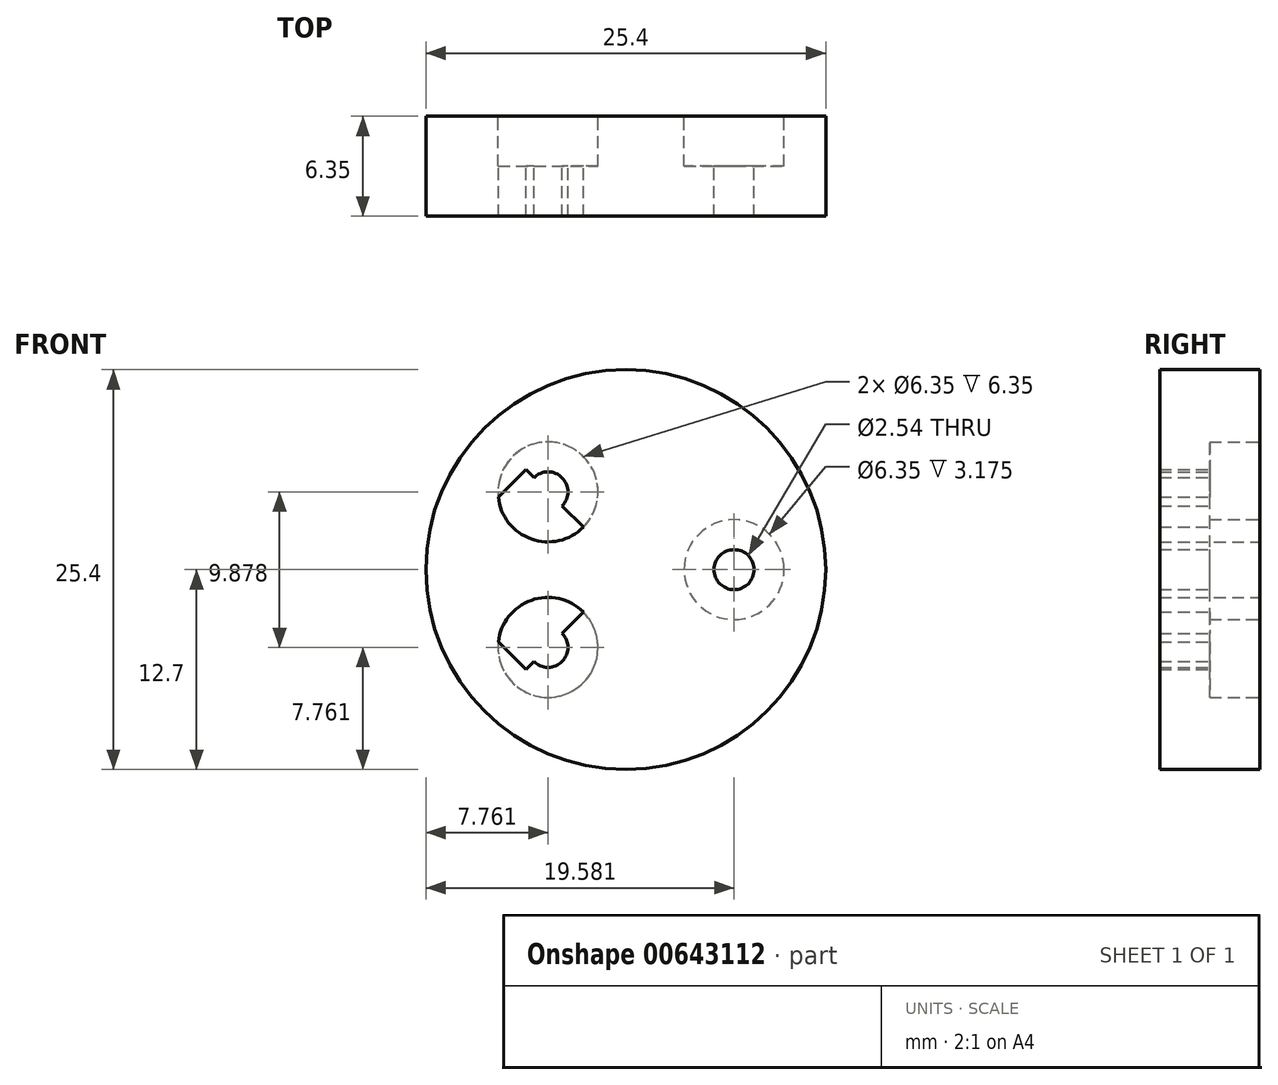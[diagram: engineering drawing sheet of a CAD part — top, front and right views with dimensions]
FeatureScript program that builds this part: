
annotation { "Feature Type Name" : "Feature", "Feature Type Description" : "" }
export const myFeature = defineFeature(function(context is Context, id is Id, definition is map)
    precondition{}
    {
        {
            var Q0;
            Q0=qCreatedBy(makeId("Front.planeOp"),FACE);
            var sketch = newSketch(context, id + "F0", { "sketchPlane" : qUnion([Q0])});
            skCircle(sketch, "E0", {"center": v(0, 0) * mm, "radius": 12.7 * mm});
            skCircle(sketch, "E1", {"center": v(-4.94, 4.94) * mm, "radius": 3.18 * mm});
            skCircle(sketch, "E2", {"center": v(-4.94, -4.94) * mm, "radius": 3.18 * mm});
            skCircle(sketch, "E3", {"center": v(6.88, 0) * mm, "radius": 3.18 * mm});
            skLineSegment(sketch, "E4", {"start": v(0, 12.7) * mm, "end": v(0, -12.7) * mm});
            skLineSegment(sketch, "E5", {"start": v(0, -12.7) * mm, "end": v(0, 0) * mm});
            skLineSegment(sketch, "E6", {"start": v(-12.7, 0) * mm, "end": v(0, 0) * mm});
            skLineSegment(sketch, "E7", {"start": v(12.7, 0) * mm, "end": v(0, 0) * mm});
            skLineSegment(sketch, "E8", {"start": v(0, 12.7) * mm, "end": v(-12.7, 0) * mm});
            skLineSegment(sketch, "E9", {"start": v(0, 0) * mm, "end": v(-6.35, 6.35) * mm});
            skLineSegment(sketch, "E10", {"start": v(-12.7, 0) * mm, "end": v(0, -12.7) * mm});
            skLineSegment(sketch, "E11", {"start": v(0, 0) * mm, "end": v(-6.35, -6.35) * mm});
            skCircle(sketch, "E12", {"center": v(-4.94, 4.94) * mm, "radius": 1.27 * mm});
            skCircle(sketch, "E13", {"center": v(6.88, 0) * mm, "radius": 1.27 * mm});
            skCircle(sketch, "E14", {"center": v(-4.94, -4.94) * mm, "radius": 1.27 * mm});
            skSolve(sketch);
        }
        {
            var Q0;
            Q0 = qSketchRegion(id + "F0", true);
            var Q1;
            {var subQ1=sQuery(id+"F0.wireOp",EDGE,"E8");var subQ5=sQuery(id+"F0.wireOp",EDGE,"E1");var subQ6=makeQuery(id+"F0.imprint","INTERSECT",VERTEX,{"disambiguationData":[OD(0.0)],"derivedFrom":[subQ5,subQ1]});Q1=makeQuery(id+"F0.imprint","IMPRINT",FACE,{"disambiguationData":[TD([[makeQuery(id+"F0.imprint","IMPRINT",EDGE,{"disambiguationData":[TD([[subQ6,-1.0]])],"derivedFrom":subQ5}),1.0]])]});}
            var Q2;
            {var subQ1=sQuery(id+"F0.wireOp",EDGE,"E8");var subQ5=sQuery(id+"F0.wireOp",EDGE,"E1");var subQ8=makeQuery(id+"F0.imprint","INTERSECT",VERTEX,{"disambiguationData":[OD(1.0)],"derivedFrom":[subQ5,subQ1]});Q2=makeQuery(id+"F0.imprint","IMPRINT",FACE,{"disambiguationData":[TD([[makeQuery(id+"F0.imprint","IMPRINT",EDGE,{"disambiguationData":[TD([[subQ8,1.0]])],"derivedFrom":subQ5}),1.0]])]});}
            var Q3;
            {var subQ0=sQuery(id+"F0.wireOp",EDGE,"E8");var subQ1=sQuery(id+"F0.wireOp",EDGE,"E1");var subQ2=makeQuery(id+"F0.imprint","INTERSECT",VERTEX,{"disambiguationData":[OD(0.0)],"derivedFrom":[subQ1,subQ0]});Q3=makeQuery(id+"F0.imprint","IMPRINT",FACE,{"disambiguationData":[TD([[makeQuery(id+"F0.imprint","IMPRINT",EDGE,{"disambiguationData":[TD([[subQ2,1.0]])],"derivedFrom":subQ1}),1.0]])]});}
            var Q4;
            {var subQ0=sQuery(id+"F0.wireOp",EDGE,"E7");var subQ1=sQuery(id+"F0.wireOp",EDGE,"E3");var subQ2=makeQuery(id+"F0.imprint","INTERSECT",VERTEX,{"disambiguationData":[OD(0.0)],"derivedFrom":[subQ1,subQ0]});Q4=makeQuery(id+"F0.imprint","IMPRINT",FACE,{"disambiguationData":[TD([[makeQuery(id+"F0.imprint","IMPRINT",EDGE,{"disambiguationData":[TD([[subQ2,-1.0]])],"derivedFrom":subQ1}),1.0]])]});}
            var Q5;
            {var subQ0=sQuery(id+"F0.wireOp",EDGE,"E7");var subQ1=sQuery(id+"F0.wireOp",EDGE,"E3");var subQ2=makeQuery(id+"F0.imprint","INTERSECT",VERTEX,{"disambiguationData":[OD(0.0)],"derivedFrom":[subQ1,subQ0]});Q5=makeQuery(id+"F0.imprint","IMPRINT",FACE,{"disambiguationData":[TD([[makeQuery(id+"F0.imprint","IMPRINT",EDGE,{"disambiguationData":[TD([[subQ2,1.0]])],"derivedFrom":subQ1}),1.0]])]});}
            var Q6;
            {var subQ0=sQuery(id+"F0.wireOp",EDGE,"E11");var subQ1=sQuery(id+"F0.wireOp",EDGE,"E2");var subQ2=makeQuery(id+"F0.imprint","INTERSECT",VERTEX,{"derivedFrom":[subQ1,subQ0]});Q6=makeQuery(id+"F0.imprint","IMPRINT",FACE,{"disambiguationData":[TD([[makeQuery(id+"F0.imprint","IMPRINT",EDGE,{"disambiguationData":[TD([[subQ2,1.0]])],"derivedFrom":subQ1}),1.0]])]});}
            var Q7;
            {var subQ1=sQuery(id+"F0.wireOp",EDGE,"E10");var subQ5=sQuery(id+"F0.wireOp",EDGE,"E2");var subQ8=makeQuery(id+"F0.imprint","INTERSECT",VERTEX,{"disambiguationData":[OD(0.0)],"derivedFrom":[subQ5,subQ1]});Q7=makeQuery(id+"F0.imprint","IMPRINT",FACE,{"disambiguationData":[TD([[makeQuery(id+"F0.imprint","IMPRINT",EDGE,{"disambiguationData":[TD([[subQ8,1.0]])],"derivedFrom":subQ5}),1.0]])]});}
            var Q8;
            {var subQ0=sQuery(id+"F0.wireOp",EDGE,"E10");var subQ1=sQuery(id+"F0.wireOp",EDGE,"E2");var subQ2=makeQuery(id+"F0.imprint","INTERSECT",VERTEX,{"disambiguationData":[OD(0.0)],"derivedFrom":[subQ1,subQ0]});Q8=makeQuery(id+"F0.imprint","IMPRINT",FACE,{"disambiguationData":[TD([[makeQuery(id+"F0.imprint","IMPRINT",EDGE,{"disambiguationData":[TD([[subQ2,-1.0]])],"derivedFrom":subQ1}),1.0]])]});}
            extrude(context, id + "F1", {"entities" : qUnion([Q0, Q1, Q2, Q3, Q4, Q5, Q6, Q7, Q8]), "depth" : 6.35 * mm, "offsetDistance" : 25.4 * mm});
        }
        {
            var Q0;
            {var subQ1=sQuery(id+"F0.wireOp",EDGE,"E8");var subQ5=sQuery(id+"F0.wireOp",EDGE,"E1");var subQ6=makeQuery(id+"F0.imprint","INTERSECT",VERTEX,{"disambiguationData":[OD(0.0)],"derivedFrom":[subQ5,subQ1]});Q0=makeQuery(id+"F0.imprint","IMPRINT",FACE,{"disambiguationData":[TD([[makeQuery(id+"F0.imprint","IMPRINT",EDGE,{"disambiguationData":[TD([[subQ6,-1.0]])],"derivedFrom":subQ5}),1.0]])]});}
            var Q1;
            {var subQ0=sQuery(id+"F0.wireOp",EDGE,"E8");var subQ1=sQuery(id+"F0.wireOp",EDGE,"E1");var subQ2=makeQuery(id+"F0.imprint","INTERSECT",VERTEX,{"disambiguationData":[OD(0.0)],"derivedFrom":[subQ1,subQ0]});Q1=makeQuery(id+"F0.imprint","IMPRINT",FACE,{"disambiguationData":[TD([[makeQuery(id+"F0.imprint","IMPRINT",EDGE,{"disambiguationData":[TD([[subQ2,1.0]])],"derivedFrom":subQ1}),1.0]])]});}
            var Q2;
            {var subQ1=sQuery(id+"F0.wireOp",EDGE,"E8");var subQ5=sQuery(id+"F0.wireOp",EDGE,"E1");var subQ8=makeQuery(id+"F0.imprint","INTERSECT",VERTEX,{"disambiguationData":[OD(1.0)],"derivedFrom":[subQ5,subQ1]});Q2=makeQuery(id+"F0.imprint","IMPRINT",FACE,{"disambiguationData":[TD([[makeQuery(id+"F0.imprint","IMPRINT",EDGE,{"disambiguationData":[TD([[subQ8,1.0]])],"derivedFrom":subQ5}),1.0]])]});}
            var Q3;
            {var subQ1=sQuery(id+"F0.wireOp",EDGE,"E10");var subQ5=sQuery(id+"F0.wireOp",EDGE,"E2");var subQ8=makeQuery(id+"F0.imprint","INTERSECT",VERTEX,{"disambiguationData":[OD(0.0)],"derivedFrom":[subQ5,subQ1]});Q3=makeQuery(id+"F0.imprint","IMPRINT",FACE,{"disambiguationData":[TD([[makeQuery(id+"F0.imprint","IMPRINT",EDGE,{"disambiguationData":[TD([[subQ8,1.0]])],"derivedFrom":subQ5}),1.0]])]});}
            var Q4;
            {var subQ0=sQuery(id+"F0.wireOp",EDGE,"E11");var subQ1=sQuery(id+"F0.wireOp",EDGE,"E2");var subQ2=makeQuery(id+"F0.imprint","INTERSECT",VERTEX,{"derivedFrom":[subQ1,subQ0]});Q4=makeQuery(id+"F0.imprint","IMPRINT",FACE,{"disambiguationData":[TD([[makeQuery(id+"F0.imprint","IMPRINT",EDGE,{"disambiguationData":[TD([[subQ2,1.0]])],"derivedFrom":subQ1}),1.0]])]});}
            var Q5;
            {var subQ0=sQuery(id+"F0.wireOp",EDGE,"E10");var subQ1=sQuery(id+"F0.wireOp",EDGE,"E2");var subQ2=makeQuery(id+"F0.imprint","INTERSECT",VERTEX,{"disambiguationData":[OD(0.0)],"derivedFrom":[subQ1,subQ0]});Q5=makeQuery(id+"F0.imprint","IMPRINT",FACE,{"disambiguationData":[TD([[makeQuery(id+"F0.imprint","IMPRINT",EDGE,{"disambiguationData":[TD([[subQ2,-1.0]])],"derivedFrom":subQ1}),1.0]])]});}
            var Q6;
            {var subQ0=sQuery(id+"F0.wireOp",EDGE,"E7");var subQ1=sQuery(id+"F0.wireOp",EDGE,"E3");var subQ2=makeQuery(id+"F0.imprint","INTERSECT",VERTEX,{"disambiguationData":[OD(0.0)],"derivedFrom":[subQ1,subQ0]});Q6=makeQuery(id+"F0.imprint","IMPRINT",FACE,{"disambiguationData":[TD([[makeQuery(id+"F0.imprint","IMPRINT",EDGE,{"disambiguationData":[TD([[subQ2,1.0]])],"derivedFrom":subQ1}),1.0]])]});}
            var Q7;
            {var subQ0=sQuery(id+"F0.wireOp",EDGE,"E7");var subQ1=sQuery(id+"F0.wireOp",EDGE,"E3");var subQ2=makeQuery(id+"F0.imprint","INTERSECT",VERTEX,{"disambiguationData":[OD(0.0)],"derivedFrom":[subQ1,subQ0]});Q7=makeQuery(id+"F0.imprint","IMPRINT",FACE,{"disambiguationData":[TD([[makeQuery(id+"F0.imprint","IMPRINT",EDGE,{"disambiguationData":[TD([[subQ2,-1.0]])],"derivedFrom":subQ1}),1.0]])]});}
            extrude(context, id + "F2", {"entities" : qUnion([Q0, Q1, Q2, Q3, Q4, Q5, Q6, Q7]), "operationType" : NewBodyOperationType.REMOVE, "depth" : 3.17 * mm, "offsetDistance" : 25.4 * mm});
        }
    });
